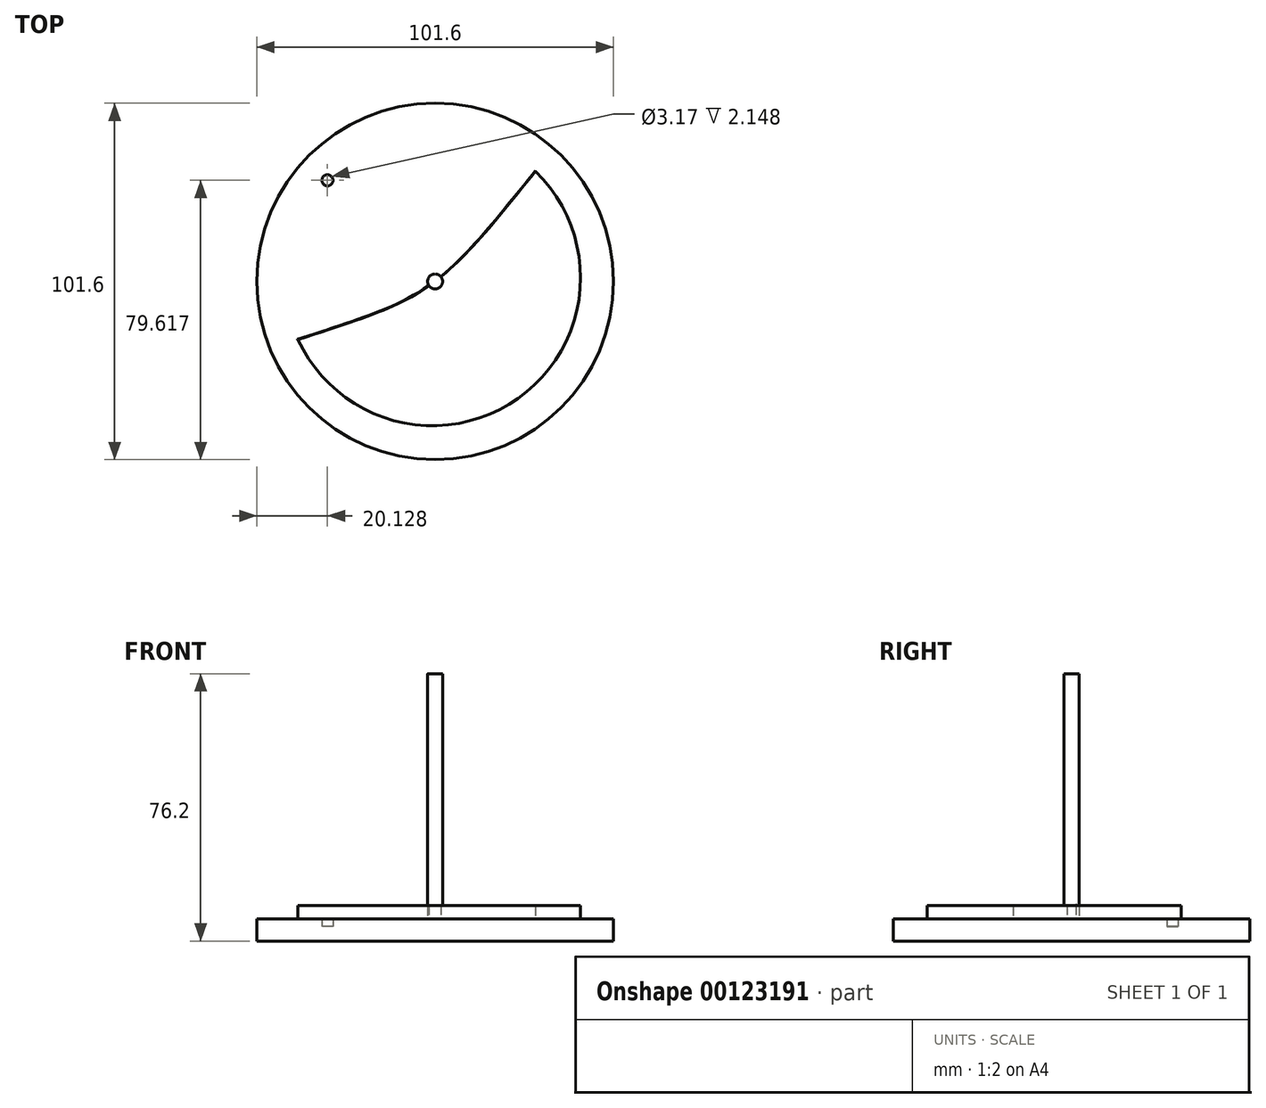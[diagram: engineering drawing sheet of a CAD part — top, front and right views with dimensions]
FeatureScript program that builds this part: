
annotation { "Feature Type Name" : "Feature", "Feature Type Description" : "" }
export const myFeature = defineFeature(function(context is Context, id is Id, definition is map)
    precondition{}
    {
        {
            var Q0;
            Q0=qCreatedBy(makeId("Top.planeOp"),FACE);
            var sketch = newSketch(context, id + "F0", { "sketchPlane" : qUnion([Q0])});
            skCircle(sketch, "E0", {"center": v(0, 0) * mm, "radius": 50.8 * mm});
            skLineSegment(sketch, "E1", {"start": v(0, 0) * mm, "end": v(-28.15, 26.49) * mm, "construction": true});
            skCircle(sketch, "E2", {"center": v(0, 0) * mm, "radius": 46.57 * mm, "construction": true});
            skCircle(sketch, "E3", {"center": v(-30.67, 28.82) * mm, "radius": 1.59 * mm});
            skSolve(sketch);
        }
        {
            var Q0;
            Q0=makeQuery(id+"F0.imprint","IMPRINT",FACE,{"disambiguationData":[TD([[makeQuery(id+"F0.imprint","IMPRINT",EDGE,{"derivedFrom":sQuery(id+"F0.wireOp",EDGE,"E0")}),1.0]])]});
            extrude(context, id + "F1", {"entities" : qUnion([Q0]), "depth" : 6.35 * mm});
        }
        {
            var Q0;
            Q0=qCreatedBy(makeId("Top.planeOp"),FACE);
            var sketch = newSketch(context, id + "F2", { "sketchPlane" : qUnion([Q0])});
            skFitSpline(sketch, "E4", {"points": [v(-39.06, -16.6) * mm, v(0, 0) * mm, v(28.6, 31.35) * mm], "startDerivative": vector(117.27, 38.4) * mm, "endDerivative": vector(64.02, 78.42) * mm});
            skArc(sketch, "E5", {"start": v(-39.06, -16.6) * mm, "mid": v(23.64, -33.36) * mm, "end": v(28.6, 31.35) * mm});
            skSolve(sketch);
        }
        {
            var Q0;
            Q0 = qSketchRegion(id + "F2", true);
            extrude(context, id + "F3", {"entities" : qUnion([Q0]), "operationType" : NewBodyOperationType.ADD, "depth" : 10.16 * mm});
        }
        {
            var Q0;
            Q0=qCreatedBy(makeId("Top.planeOp"),FACE);
            var sketch = newSketch(context, id + "F4", { "sketchPlane" : qUnion([Q0])});
            skCircle(sketch, "E6", {"center": v(0, 0) * mm, "radius": 2.13 * mm});
            skSolve(sketch);
        }
        {
            var Q0;
            Q0 = qSketchRegion(id + "F4", true);
            extrude(context, id + "F5", {"entities" : qUnion([Q0]), "operationType" : NewBodyOperationType.ADD, "depth" : 76.2 * mm});
        }
        {
            var Q0;
            Q0=makeQuery(id+"F5.boolean.opBoolean","INTERSECT",EDGE,{"derivedFrom":[makeQuery(id+"F3.opExtrude","CAP_FACE",FACE,{"disambiguationData":[OSD([sQuery(id+"F2.wireOp",EDGE,"TA63iwTC-EfHz-3AYF-eTuh-UPEtw5TZPom2"),sQuery(id+"F2.wireOp",EDGE,"E4")])],"isStart":false}),makeQuery(id+"F5.opExtrude","SWEPT_FACE",FACE,{"disambiguationData":[OSD([sQuery(id+"F4.wireOp",EDGE,"E6")])]})]});
            fillet(context, id + "F6", {"entities" : qUnion([Q0]), "radius" : 0.28 * mm, "tangentPropagation" : true, "rho" : 0.5, "crossSection" : FilletCrossSection.CONIC, "allowEdgeOverflow" : false});
        }
        {
            var Q0;
            Q0=makeQuery(id+"F0.imprint","IMPRINT",FACE,{"disambiguationData":[TD([[makeQuery(id+"F0.imprint","IMPRINT",EDGE,{"derivedFrom":sQuery(id+"F0.wireOp",EDGE,"E3")}),1.0]])]});
            extrude(context, id + "F7", {"entities" : qUnion([Q0]), "operationType" : NewBodyOperationType.ADD, "depth" : 4.2 * mm});
        }
        {
            var Q0;
            Q0=makeQuery(id+"F3.boolean.opBoolean","INTERSECT",EDGE,{"derivedFrom":[makeQuery(id+"F1.opExtrude","CAP_FACE",FACE,{"disambiguationData":[OSD([sQuery(id+"F0.wireOp",EDGE,"E0"),sQuery(id+"F0.wireOp",EDGE,"E3")])],"isStart":false}),makeQuery(id+"F3.opExtrude","SWEPT_FACE",FACE,{"disambiguationData":[OSD([sQuery(id+"F2.wireOp",EDGE,"E5")])]})]});
            var Q1;
            Q1=makeQuery(id+"F5.boolean.opBoolean","SPLIT",EDGE,{"disambiguationData":[OD(0.0)],"derivedFrom":makeQuery(id+"F3.boolean.opBoolean","INTERSECT",EDGE,{"derivedFrom":[makeQuery(id+"F1.opExtrude","CAP_FACE",FACE,{"disambiguationData":[OSD([sQuery(id+"F0.wireOp",EDGE,"E0"),sQuery(id+"F0.wireOp",EDGE,"E3")])],"isStart":false}),makeQuery(id+"F3.opExtrude","SWEPT_FACE",FACE,{"disambiguationData":[OSD([sQuery(id+"F2.wireOp",EDGE,"E4")])]})]})});
            var Q2;
            Q2=makeQuery(id+"F5.boolean.opBoolean","SPLIT",EDGE,{"disambiguationData":[OD(1.0)],"derivedFrom":makeQuery(id+"F3.boolean.opBoolean","INTERSECT",EDGE,{"derivedFrom":[makeQuery(id+"F1.opExtrude","CAP_FACE",FACE,{"disambiguationData":[OSD([sQuery(id+"F0.wireOp",EDGE,"E0"),sQuery(id+"F0.wireOp",EDGE,"E3")])],"isStart":false}),makeQuery(id+"F3.opExtrude","SWEPT_FACE",FACE,{"disambiguationData":[OSD([sQuery(id+"F2.wireOp",EDGE,"E4")])]})]})});
            var Q3;
            Q3=makeQuery(id+"F5.boolean.opBoolean","INTERSECT",EDGE,{"derivedFrom":[makeQuery(id+"F1.opExtrude","CAP_FACE",FACE,{"disambiguationData":[OSD([sQuery(id+"F0.wireOp",EDGE,"E0"),sQuery(id+"F0.wireOp",EDGE,"E3")])],"isStart":false}),makeQuery(id+"F5.opExtrude","SWEPT_FACE",FACE,{"disambiguationData":[OSD([sQuery(id+"F4.wireOp",EDGE,"E6")])]})]});
            fillet(context, id + "F8", {"entities" : qUnion([Q0, Q1, Q2, Q3]), "radius" : 0.1 * mm, "tangentPropagation" : true, "rho" : 0.5, "crossSection" : FilletCrossSection.CONIC, "allowEdgeOverflow" : false});
        }
    });
